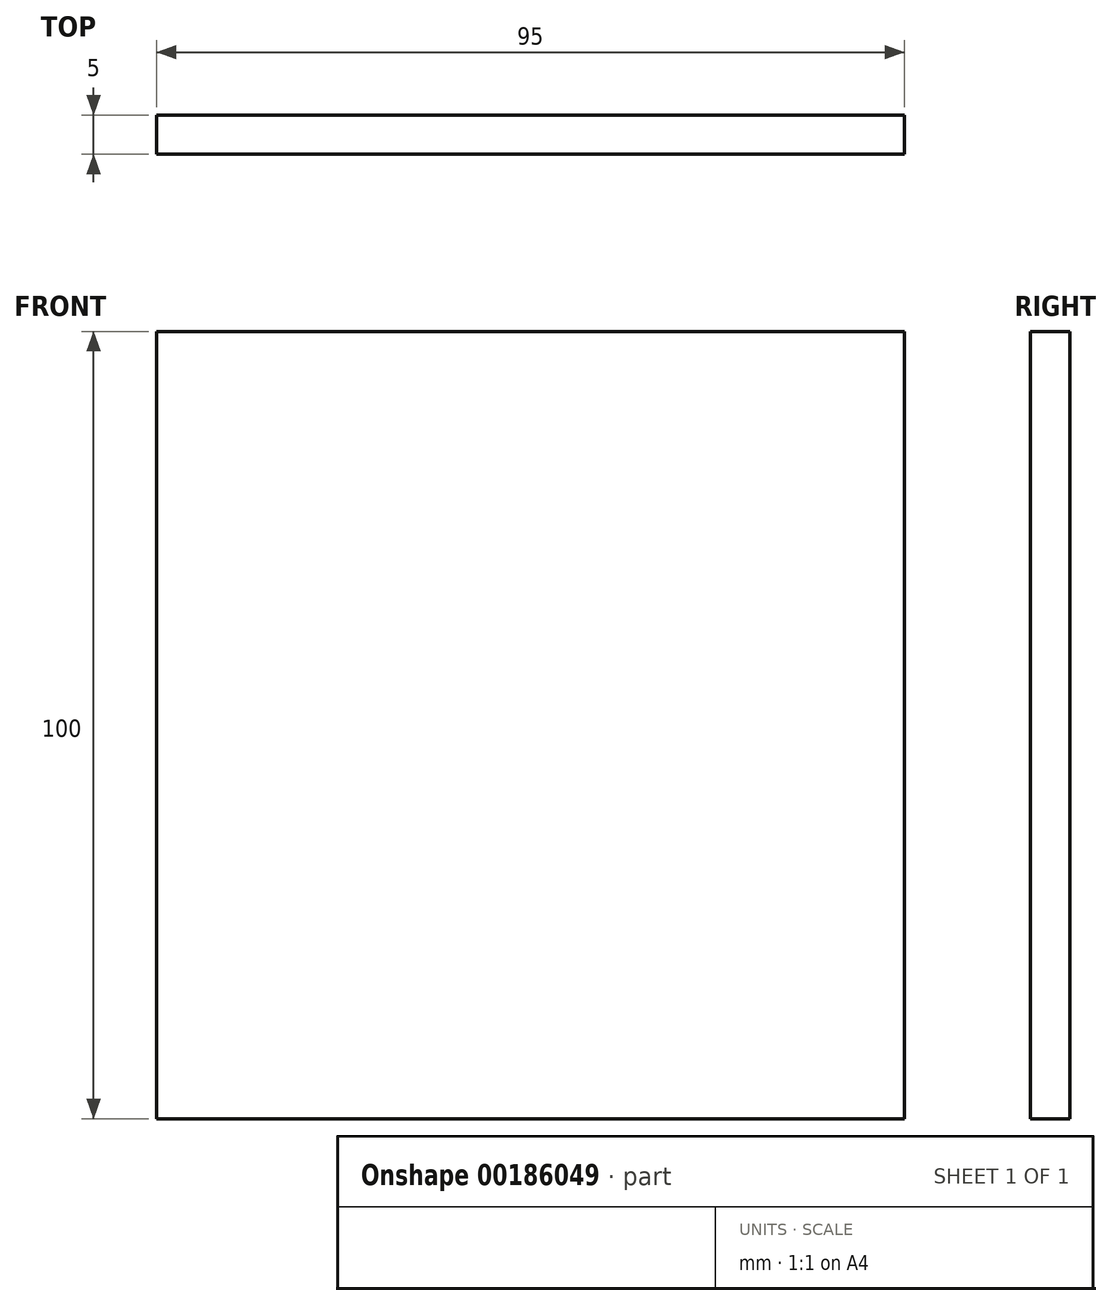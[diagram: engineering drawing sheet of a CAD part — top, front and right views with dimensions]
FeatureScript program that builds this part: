
annotation { "Feature Type Name" : "Feature", "Feature Type Description" : "" }
export const myFeature = defineFeature(function(context is Context, id is Id, definition is map)
    precondition{}
    {
        {
            var Q0;
            Q0=qCreatedBy(makeId("Front.planeOp"),FACE);
            var sketch = newSketch(context, id + "F0", { "sketchPlane" : qUnion([Q0])});
            skLineSegment(sketch, "E0.bottom", {"start": v(5, 0) * mm, "end": v(100, 0) * mm});
            skLineSegment(sketch, "E0.top", {"start": v(5, 100) * mm, "end": v(100, 100) * mm});
            skLineSegment(sketch, "E0.left", {"start": v(5, 0) * mm, "end": v(5, 100) * mm});
            skLineSegment(sketch, "E0.right", {"start": v(100, 0) * mm, "end": v(100, 100) * mm});
            skSolve(sketch);
        }
        {
            var Q0;
            Q0=makeQuery(id+"F0.imprint","IMPRINT",FACE,{"disambiguationData":[TD([[makeQuery(id+"F0.imprint","IMPRINT",EDGE,{"derivedFrom":sQuery(id+"F0.wireOp",EDGE,"E0.bottom")}),1.0]])]});
            extrude(context, id + "F1", {"entities" : qUnion([Q0]), "endBound" : BoundingType.SYMMETRIC, "depth" : 5 * mm});
        }
    });
